# Revit family: DLC-PC
name_source: partatom
category: Communication Devices
revit_build: Autodesk Revit 2014 (Build: 20130308_1515(x64)
units: mm (PartAtom-declared; Revit-internal decimal feet)

## types (1)
- DLC-PC
    Assembly Code = D5090
    Certifications = ETL/UL 916 Listed
Title 24 Listed
RoHS compliant
    Default Elevation = 48 "
    Description = The Lux Meter/Photo Sensor provides the necessary daylight-level information to the Fixture Module. Using a photodiode element, this sensor continuously measures daylight levels and sends the information to the fixture module.
    Features = Continuous dim operation with 0-10V output
• Foot-candle range: 0-250FC
• Mounts horizontally
• UL and cUL listed
• California Title 24 Compliant
• Five-year limited warranty
• Low voltage device: 24 VDC
    Gray = Paint - Hubbell - Gray Smooth
    Height = 4.5 "
    Manufacturer = Hubbell Control Solutions
    Metal = Gold
    Model = DLC-PC
    Product Documentation Link = https://hubbellcdn.com
    Product Page URL = https://www.hubbell.com
    Sensing Element = Paint - Hubbell - Matte White
    Type Comments = Outdoor Lux Meter Sensor
    URL = https://www.hubbell.com
    Warranty = 5-Years Warranty
    Width = 2 "

## geometry (parser evidence)
native form markers: Sweep x1
no freeform markers — native parametric forms only
